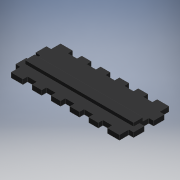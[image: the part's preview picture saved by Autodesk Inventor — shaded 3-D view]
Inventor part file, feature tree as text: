
AUTODESK INVENTOR PART (.ipt)
format: ipt  version: 2019 (Build 230136000, 136)  size: 207,872 bytes
history: native  units: mm
features: extrude x3, sketch x3, projected_geometry x1
ambient origin geometry x8: Origin, YZ Plane, XZ Plane, XY Plane, X Axis, Y Axis, Z Axis, Center Point
bodies: Solid1 (feature_tree)
feature tree (7):
  extrude  "Extrusion1"  Depth=42.0mm
  extrude  "Extrusion2"  Depth=4.0mm
  extrude  "Extrusion3"  Depth=8.0mm
  sketch  "Sketch1"  dims[d0=100.0mm d1=42.0mm]
  sketch  "Sketch2"  dims[d2=4.0mm d3=0.0mm d4=4.0mm]
  projected_geometry  "Projected Loop1"
  sketch  "Sketch3"  dims[d5=4.0mm d7=8.0mm d8=8.0mm d10=8.0mm d11=8.0mm d13=4.0mm d14=8.0mm d15=4.0mm d16=0.0mm d17=8.0mm d18=8.0mm d19=3.0mm d20=0.0mm]
